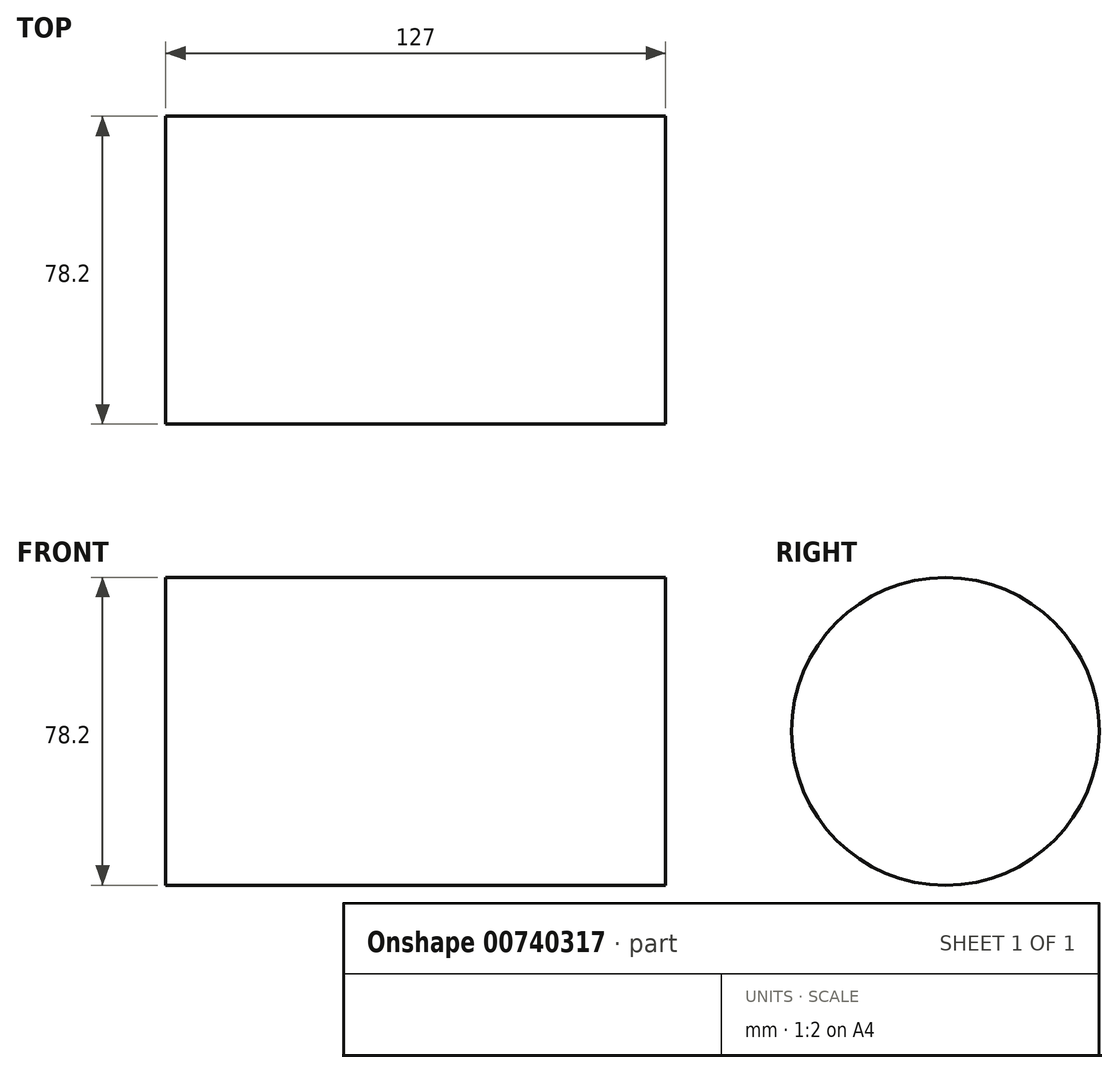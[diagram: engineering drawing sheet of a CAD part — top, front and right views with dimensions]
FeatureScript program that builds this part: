
annotation { "Feature Type Name" : "Feature", "Feature Type Description" : "" }
export const myFeature = defineFeature(function(context is Context, id is Id, definition is map)
    precondition{}
    {
        {
            var Q0;
            Q0=qCreatedBy(makeId("Right.planeOp"),FACE);
            var sketch = newSketch(context, id + "F0", { "sketchPlane" : qUnion([Q0])});
            skCircle(sketch, "E0", {"center": v(0, 0) * mm, "radius": 39.1 * mm});
            skSolve(sketch);
        }
        {
            var Q0;
            Q0=makeQuery(id+"F0.imprint","IMPRINT",FACE,{"disambiguationData":[TD([[makeQuery(id+"F0.imprint","IMPRINT",EDGE,{"derivedFrom":sQuery(id+"F0.wireOp",EDGE,"E0")}),1.0]])]});
            extrude(context, id + "F1", {"entities" : qUnion([Q0]), "depth" : 127 * mm, "offsetDistance" : 25.4 * mm});
        }
    });
